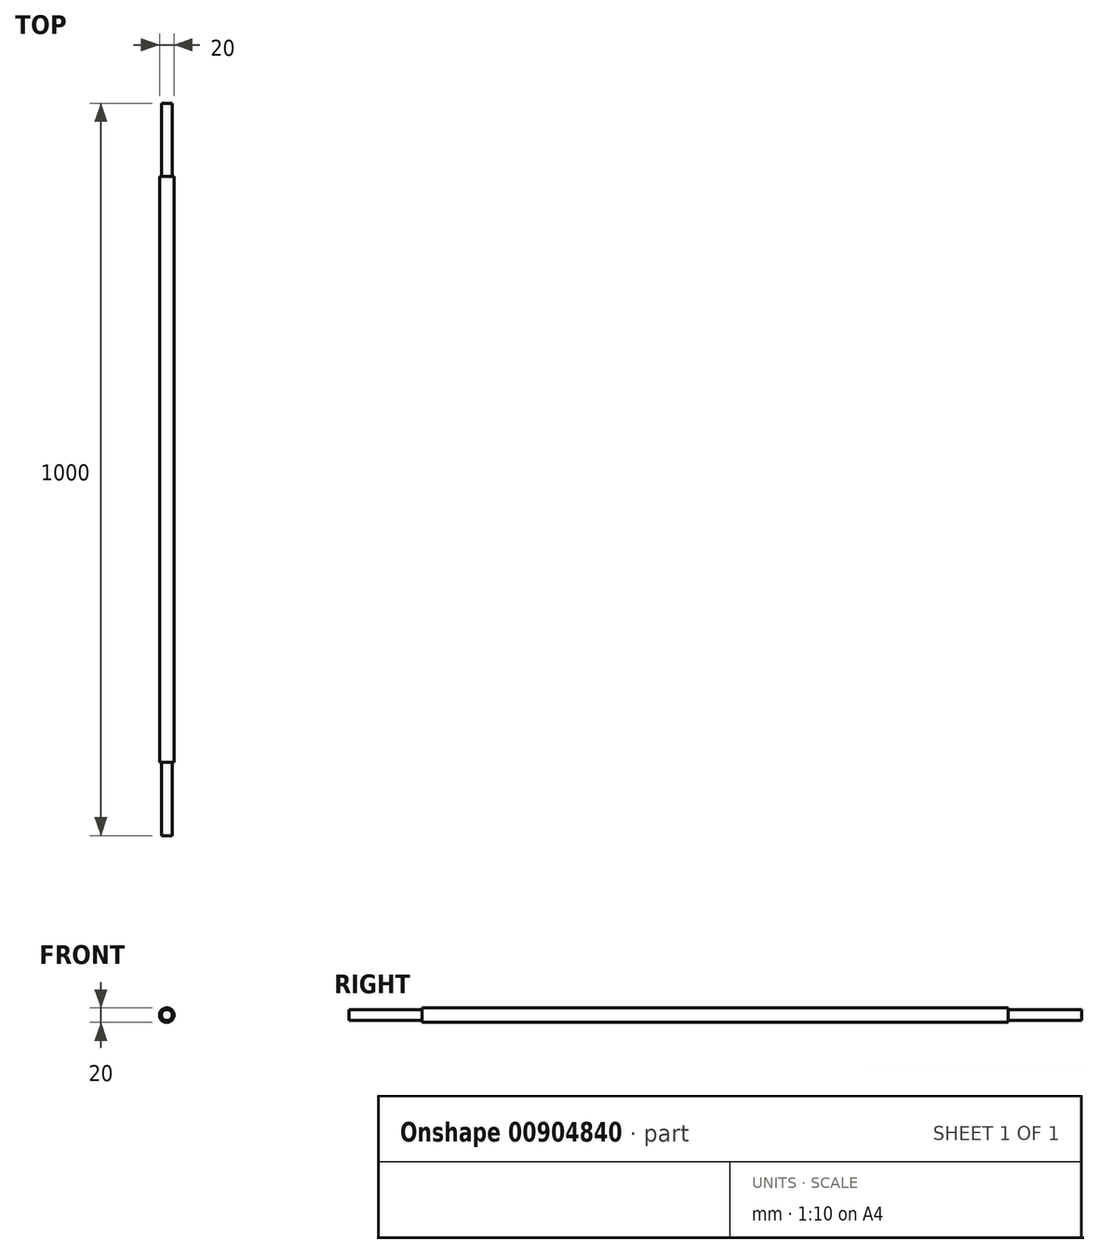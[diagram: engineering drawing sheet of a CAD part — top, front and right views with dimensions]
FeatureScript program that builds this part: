
annotation { "Feature Type Name" : "Feature", "Feature Type Description" : "" }
export const myFeature = defineFeature(function(context is Context, id is Id, definition is map)
    precondition{}
    {
        {
            var Q0;
            Q0=qCreatedBy(makeId("Front.planeOp"),FACE);
            var sketch = newSketch(context, id + "F0", { "sketchPlane" : qUnion([Q0])});
            skCircle(sketch, "E0", {"center": v(0, 0) * mm, "radius": 10 * mm});
            skSolve(sketch);
        }
        {
            var Q0;
            Q0=makeQuery(id+"F0.imprint","IMPRINT",FACE,{"disambiguationData":[TD([[makeQuery(id+"F0.imprint","IMPRINT",EDGE,{"derivedFrom":sQuery(id+"F0.wireOp",EDGE,"E0")}),1.0]])]});
            extrude(context, id + "F1", {"entities" : qUnion([Q0]), "depth" : 500 * mm, "offsetDistance" : 25 * mm});
        }
        {
            var Q0;
            Q0=makeQuery(id+"F1.opExtrude","CAP_FACE",FACE,{"disambiguationData":[OSD([sQuery(id+"F0.wireOp",EDGE,"E0")])],"isStart":true});
            extrude(context, id + "F2", {"entities" : qUnion([Q0]), "operationType" : NewBodyOperationType.ADD, "depth" : 500 * mm, "offsetDistance" : 25 * mm});
        }
        {
            var Q0;
            Q0=makeQuery(id+"F2.opExtrude","CAP_FACE",FACE,{"disambiguationData":[OSD([sQuery(id+"F0.wireOp",EDGE,"E0")])],"isStart":false});
            var sketch = newSketch(context, id + "F3", { "sketchPlane" : qUnion([Q0])});
            skCircle(sketch, "E1", {"center": v(0, 0) * mm, "radius": 7.5 * mm});
            skSolve(sketch);
        }
        {
            var Q0;
            Q0=makeQuery(id+"F3.imprint","IMPRINT",FACE,{"disambiguationData":[TD([[makeQuery(id+"F3.imprint","IMPRINT",EDGE,{"derivedFrom":sQuery(id+"F3.wireOp",EDGE,"E1")}),-1.0]])]});
            extrude(context, id + "F4", {"entities" : qUnion([Q0]), "operationType" : NewBodyOperationType.REMOVE, "oppositeDirection" : true, "depth" : 100 * mm, "offsetDistance" : 25 * mm});
        }
        {
            var Q0;
            Q0=makeQuery(id+"F1.opExtrude","CAP_FACE",FACE,{"disambiguationData":[OSD([sQuery(id+"F0.wireOp",EDGE,"E0")])],"isStart":false});
            var sketch = newSketch(context, id + "F5", { "sketchPlane" : qUnion([Q0])});
            skCircle(sketch, "E2", {"center": v(0, 0) * mm, "radius": 7.5 * mm});
            skSolve(sketch);
        }
        {
            var Q0;
            Q0=makeQuery(id+"F5.imprint","IMPRINT",FACE,{"disambiguationData":[TD([[makeQuery(id+"F5.imprint","IMPRINT",EDGE,{"derivedFrom":sQuery(id+"F5.wireOp",EDGE,"E2")}),-1.0]])]});
            extrude(context, id + "F6", {"entities" : qUnion([Q0]), "operationType" : NewBodyOperationType.REMOVE, "oppositeDirection" : true, "depth" : 100 * mm, "offsetDistance" : 25 * mm});
        }
    });
